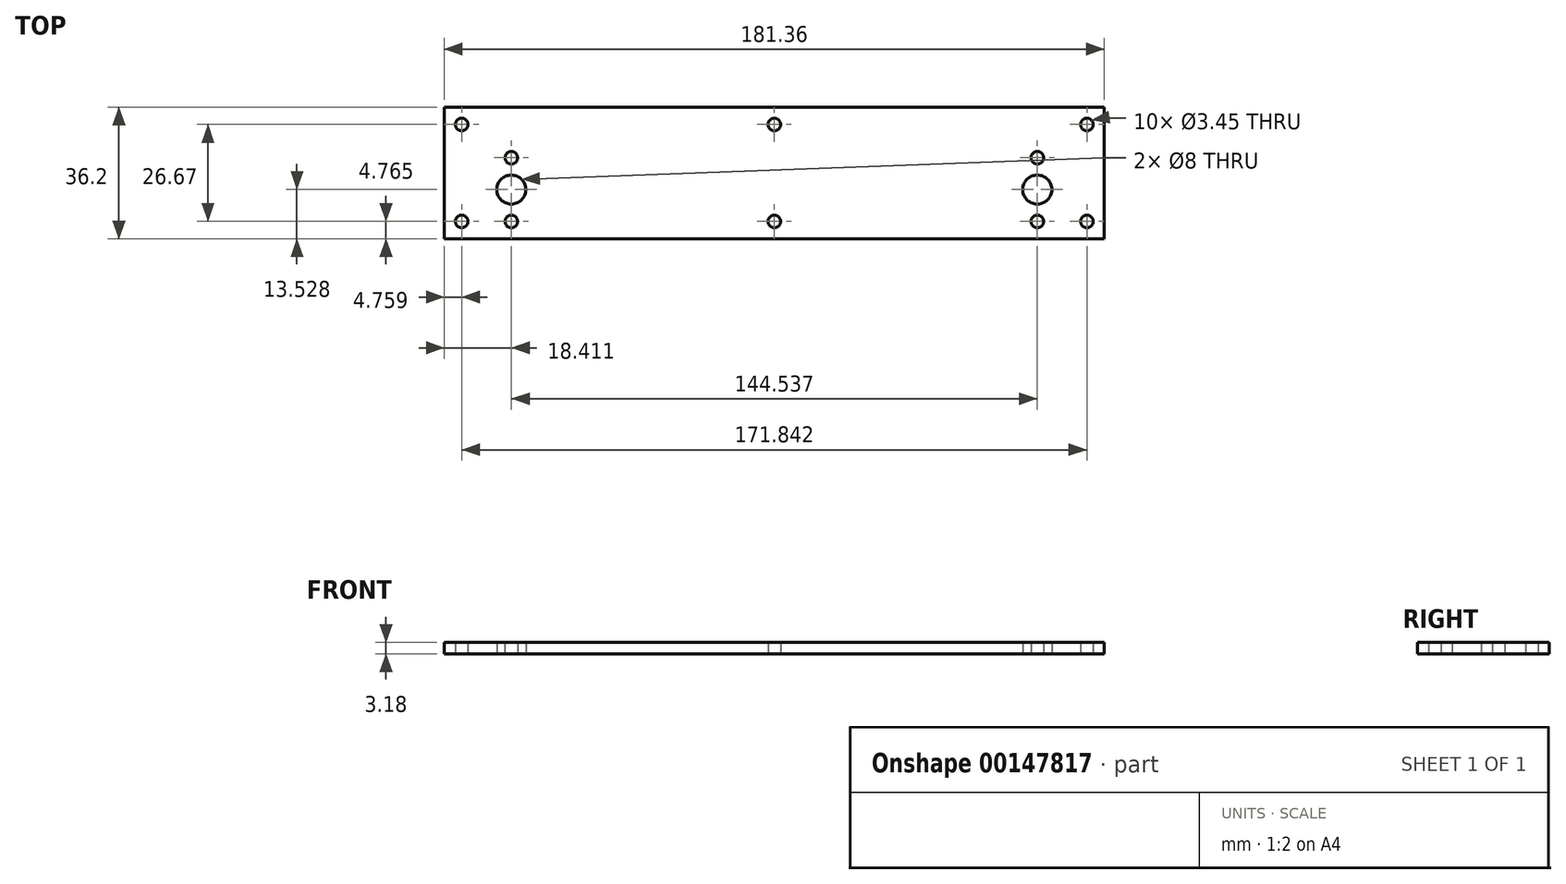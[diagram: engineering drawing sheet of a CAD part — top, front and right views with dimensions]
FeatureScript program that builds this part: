
annotation { "Feature Type Name" : "Feature", "Feature Type Description" : "" }
export const myFeature = defineFeature(function(context is Context, id is Id, definition is map)
    precondition{}
    {
        {
            var Q0;
            Q0=qCreatedBy(makeId("Top.planeOp"),FACE);
            var sketch = newSketch(context, id + "F0", { "sketchPlane" : qUnion([Q0])});
            skLineSegment(sketch, "E0.bottom", {"start": v(90.68, -18.1) * mm, "end": v(-90.68, -18.1) * mm});
            skLineSegment(sketch, "E0.top", {"start": v(90.68, 18.1) * mm, "end": v(-90.68, 18.1) * mm});
            skLineSegment(sketch, "E0.left", {"start": v(90.68, -18.1) * mm, "end": v(90.68, 18.1) * mm});
            skLineSegment(sketch, "E0.right", {"start": v(-90.68, -18.1) * mm, "end": v(-90.68, 18.1) * mm});
            skPoint(sketch, "E0.middle", {"position": v(0, 0) * mm});
            skLineSegment(sketch, "E1.bottom", {"start": v(85.92, -13.34) * mm, "end": v(-85.92, -13.34) * mm, "construction": true});
            skLineSegment(sketch, "E1.top", {"start": v(85.92, 13.34) * mm, "end": v(-85.92, 13.34) * mm, "construction": true});
            skLineSegment(sketch, "E1.left", {"start": v(85.92, -13.34) * mm, "end": v(85.92, 13.34) * mm, "construction": true});
            skLineSegment(sketch, "E1.right", {"start": v(-85.92, -13.34) * mm, "end": v(-85.92, 13.34) * mm, "construction": true});
            skLineSegment(sketch, "E2", {"start": v(-85.92, -13.34) * mm, "end": v(-85.92, -18.1) * mm, "construction": true});
            skLineSegment(sketch, "E3", {"start": v(-85.92, -13.34) * mm, "end": v(-90.68, -13.34) * mm, "construction": true});
            skCircle(sketch, "E4", {"center": v(-85.92, 13.34) * mm, "radius": 1.73 * mm});
            skCircle(sketch, "E5", {"center": v(-85.92, -13.34) * mm, "radius": 1.73 * mm});
            skCircle(sketch, "E6", {"center": v(85.92, -13.34) * mm, "radius": 1.73 * mm});
            skCircle(sketch, "E7", {"center": v(85.92, 13.34) * mm, "radius": 1.73 * mm});
            skCircle(sketch, "E8", {"center": v(0, 13.34) * mm, "radius": 1.73 * mm});
            skCircle(sketch, "E9", {"center": v(0, -13.34) * mm, "radius": 1.73 * mm});
            skLineSegment(sketch, "E10", {"start": v(0, -4.57) * mm, "end": v(0, 0) * mm, "construction": true});
            skLineSegment(sketch, "E11", {"start": v(-72.27, -4.57) * mm, "end": v(72.27, -4.57) * mm, "construction": true});
            skLineSegment(sketch, "E12", {"start": v(-72.27, 4.2) * mm, "end": v(-72.27, -13.34) * mm, "construction": true});
            skCircle(sketch, "E13", {"center": v(-72.27, 4.2) * mm, "radius": 1.73 * mm});
            skCircle(sketch, "E14", {"center": v(-72.27, -13.34) * mm, "radius": 1.73 * mm});
            skLineSegment(sketch, "E15", {"start": v(72.27, 4.2) * mm, "end": v(72.27, -13.34) * mm, "construction": true});
            skCircle(sketch, "E16", {"center": v(72.27, 4.2) * mm, "radius": 1.73 * mm});
            skCircle(sketch, "E17", {"center": v(72.27, -13.34) * mm, "radius": 1.73 * mm});
            skCircle(sketch, "E18", {"center": v(-72.27, -4.57) * mm, "radius": 4 * mm});
            skCircle(sketch, "E19", {"center": v(72.27, -4.57) * mm, "radius": 4 * mm});
            skSolve(sketch);
        }
        {
            var Q0;
            Q0=qSketchRegion(id+"F0",true);
            extrude(context, id + "F1", {"entities" : qUnion([Q0]), "depth" : 3.17 * mm});
        }
    });
